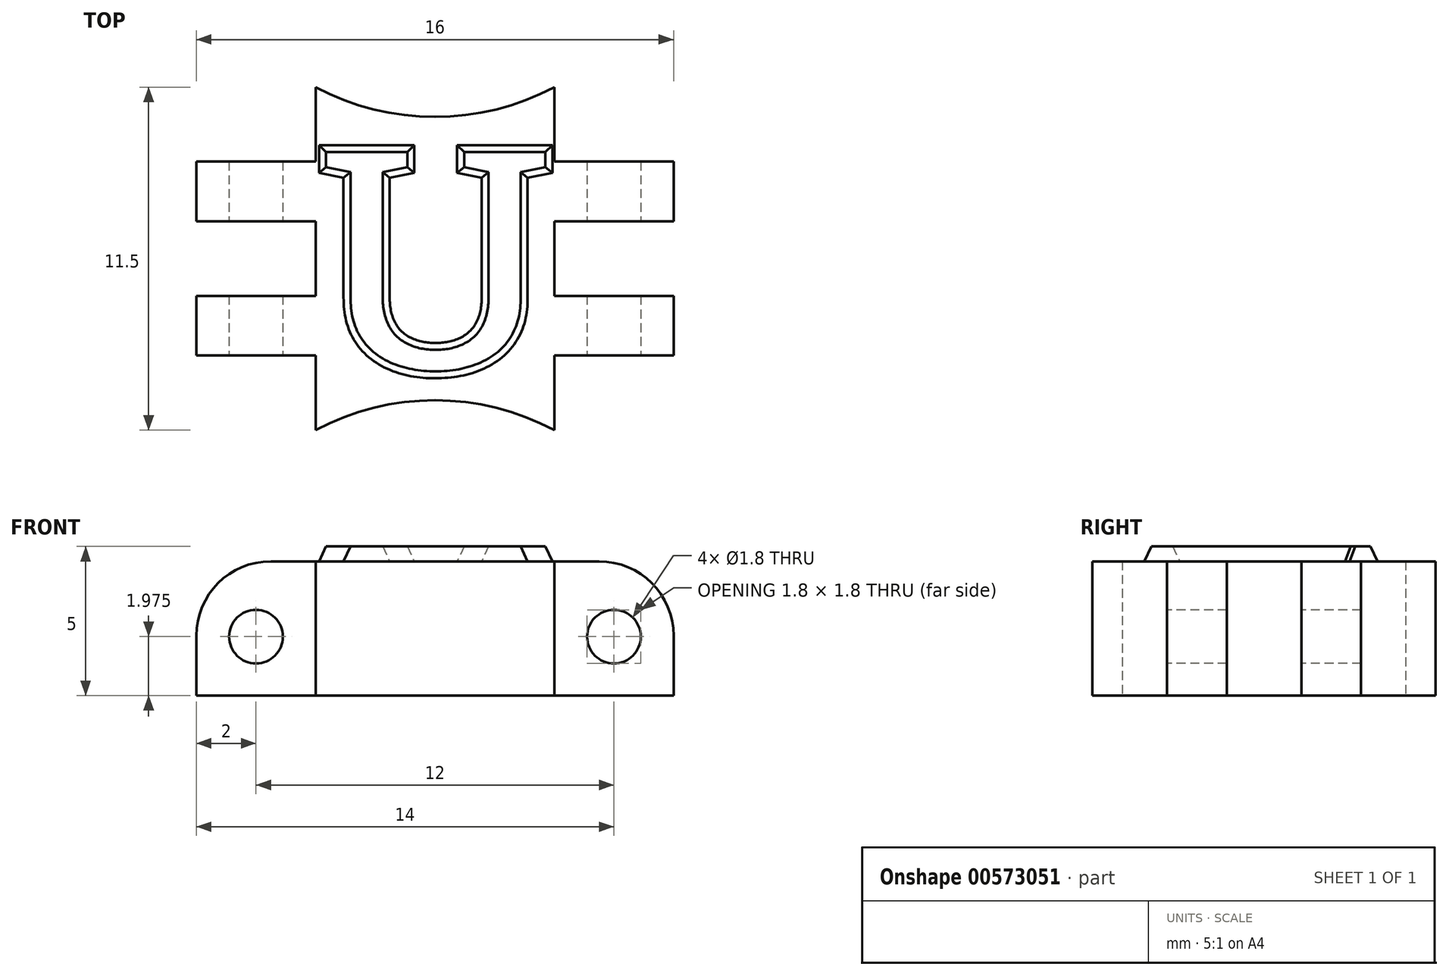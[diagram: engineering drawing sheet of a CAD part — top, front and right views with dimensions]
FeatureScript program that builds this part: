
annotation { "Feature Type Name" : "Feature", "Feature Type Description" : "" }
export const myFeature = defineFeature(function(context is Context, id is Id, definition is map)
    precondition{}
    {
        {
            var Q0;
            Q0=qCreatedBy(makeId("Top.planeOp"),FACE);
            var sketch = newSketch(context, id + "F0", { "sketchPlane" : qUnion([Q0])});
            skLineSegment(sketch, "E0", {"start": v(0, 0) * mm, "end": v(0, 9.5) * mm, "construction": true});
            skLineSegment(sketch, "E1", {"start": v(0, 9.5) * mm, "end": v(5.27, 9.5) * mm, "construction": true});
            skArc(sketch, "E2", {"start": v(0, 9.5) * mm, "mid": v(-2.06, 9.75) * mm, "end": v(-4, 10.5) * mm});
            skLineSegment(sketch, "E3", {"start": v(-4, 10.5) * mm, "end": v(-4, 8) * mm});
            skLineSegment(sketch, "E4", {"start": v(-4, 8) * mm, "end": v(-8, 8) * mm});
            skLineSegment(sketch, "E5", {"start": v(-8, 8) * mm, "end": v(-8, 6) * mm});
            skLineSegment(sketch, "E6", {"start": v(-8, 6) * mm, "end": v(-4, 6) * mm});
            skLineSegment(sketch, "E7", {"start": v(-4, 6) * mm, "end": v(-4, 3.5) * mm});
            skLineSegment(sketch, "E8", {"start": v(-4, 3.5) * mm, "end": v(-8, 3.5) * mm});
            skLineSegment(sketch, "E9", {"start": v(-8, 3.5) * mm, "end": v(-8, 1.5) * mm});
            skLineSegment(sketch, "E10", {"start": v(-8, 1.5) * mm, "end": v(-4, 1.5) * mm});
            skLineSegment(sketch, "E11", {"start": v(-4, 1.5) * mm, "end": v(-4, -1) * mm});
            skLineSegment(sketch, "E12", {"start": v(0, 0) * mm, "end": v(6.13, 0) * mm, "construction": true});
            skArc(sketch, "E13", {"start": v(0, 0) * mm, "mid": v(-2.06, -0.25) * mm, "end": v(-4, -1) * mm});
            skLineSegment(sketch, "E14", {"start": v(0, 4.75) * mm, "end": v(-4, 4.75) * mm, "construction": true});
            skArc(sketch, "E15.MirrorCS", {"start": v(0, 0) * mm, "mid": v(2.06, -0.25) * mm, "end": v(4, -1) * mm});
            skLineSegment(sketch, "E16.MirrorCS", {"start": v(4, 1.5) * mm, "end": v(4, -1) * mm});
            skLineSegment(sketch, "E17.MirrorCS", {"start": v(8, 1.5) * mm, "end": v(4, 1.5) * mm});
            skLineSegment(sketch, "E18.MirrorCS", {"start": v(8, 3.5) * mm, "end": v(8, 1.5) * mm});
            skLineSegment(sketch, "E19.MirrorCS", {"start": v(4, 3.5) * mm, "end": v(8, 3.5) * mm});
            skLineSegment(sketch, "E20.MirrorCS", {"start": v(4, 6) * mm, "end": v(4, 3.5) * mm});
            skLineSegment(sketch, "E21.MirrorCS", {"start": v(8, 6) * mm, "end": v(4, 6) * mm});
            skLineSegment(sketch, "E22.MirrorCS", {"start": v(8, 8) * mm, "end": v(8, 6) * mm});
            skLineSegment(sketch, "E23.MirrorCS", {"start": v(4, 8) * mm, "end": v(8, 8) * mm});
            skLineSegment(sketch, "E24.MirrorCS", {"start": v(4, 10.5) * mm, "end": v(4, 8) * mm});
            skArc(sketch, "E25.MirrorCS", {"start": v(0, 9.5) * mm, "mid": v(2.06, 9.75) * mm, "end": v(4, 10.5) * mm});
            skSolve(sketch);
        }
        {
            var Q0;
            Q0 = qSketchRegion(id + "F0", true);
            extrude(context, id + "F1", {"entities" : qUnion([Q0]), "depth" : 4.5 * mm, "offsetDistance" : 25 * mm});
        }
        {
            var Q0;
            Q0=makeQuery(id+"F1.opExtrude","CAP_EDGE",EDGE,{"disambiguationData":[OSD([sQuery(id+"F0.wireOp",EDGE,"E5")])],"isStart":false});
            var Q1;
            Q1=makeQuery(id+"F1.opExtrude","CAP_EDGE",EDGE,{"disambiguationData":[OSD([sQuery(id+"F0.wireOp",EDGE,"E22.MirrorCS")])],"isStart":false});
            var Q2;
            Q2=makeQuery(id+"F1.opExtrude","CAP_EDGE",EDGE,{"disambiguationData":[OSD([sQuery(id+"F0.wireOp",EDGE,"E9")])],"isStart":false});
            var Q3;
            Q3=makeQuery(id+"F1.opExtrude","CAP_EDGE",EDGE,{"disambiguationData":[OSD([sQuery(id+"F0.wireOp",EDGE,"E18.MirrorCS")])],"isStart":false});
            fillet(context, id + "F2", {"entities" : qUnion([Q0, Q1, Q2, Q3]), "radius" : 2.5 * mm, "tangentPropagation" : true, "allowEdgeOverflow" : false});
        }
        {
            var Q0;
            Q0=makeQuery(id+"F1.opExtrude","CAP_FACE",FACE,{"disambiguationData":[OSD([sQuery(id+"F0.wireOp",EDGE,"E2"),sQuery(id+"F0.wireOp",EDGE,"E3"),sQuery(id+"F0.wireOp",EDGE,"E4"),sQuery(id+"F0.wireOp",EDGE,"E5"),sQuery(id+"F0.wireOp",EDGE,"E6"),sQuery(id+"F0.wireOp",EDGE,"E7"),sQuery(id+"F0.wireOp",EDGE,"E8"),sQuery(id+"F0.wireOp",EDGE,"E9"),sQuery(id+"F0.wireOp",EDGE,"E10"),sQuery(id+"F0.wireOp",EDGE,"E11"),sQuery(id+"F0.wireOp",EDGE,"E13"),sQuery(id+"F0.wireOp",EDGE,"E15.MirrorCS"),sQuery(id+"F0.wireOp",EDGE,"E16.MirrorCS"),sQuery(id+"F0.wireOp",EDGE,"E17.MirrorCS"),sQuery(id+"F0.wireOp",EDGE,"E18.MirrorCS"),sQuery(id+"F0.wireOp",EDGE,"E19.MirrorCS"),sQuery(id+"F0.wireOp",EDGE,"E20.MirrorCS"),sQuery(id+"F0.wireOp",EDGE,"E21.MirrorCS"),sQuery(id+"F0.wireOp",EDGE,"E22.MirrorCS"),sQuery(id+"F0.wireOp",EDGE,"E23.MirrorCS"),sQuery(id+"F0.wireOp",EDGE,"E24.MirrorCS"),sQuery(id+"F0.wireOp",EDGE,"E25.MirrorCS")])],"isStart":false});
            var sketch = newSketch(context, id + "F3", { "sketchPlane" : qUnion([Q0])});
            skText(sketch, "E26", { "text": "U", "fontName": "RobotoSlab-Bold.ttf"});
            skLineSegment(sketch, "E27", {"start": v(0.68, 8.48) * mm, "end": v(-0.68, 8.48) * mm});
            skLineSegment(sketch, "E28", {"start": v(0, 8.48) * mm, "end": v(0, 0) * mm, "construction": true});
            const initialGuessF3  = {"E26": [-0.00409, 0.00085, 1, 0, 0.0078]};
            skSetInitialGuess(sketch, initialGuessF3);
            skSolve(sketch);
        }
        {
            var Q0;
            Q0 = qSketchRegion(id + "F3", true);
            extrude(context, id + "F4", {"entities" : qUnion([Q0]), "operationType" : NewBodyOperationType.ADD, "depth" : 0.5 * mm, "offsetDistance" : 25 * mm, "hasDraft" : true, "draftAngle" : 25 * degree, "draftPullDirection" : true});
        }
        {
            var Q0;
            Q0=makeQuery(id+"F1.opExtrude","SWEPT_FACE",FACE,{"disambiguationData":[OSD([sQuery(id+"F0.wireOp",EDGE,"E10")])]});
            var sketch = newSketch(context, id + "F5", { "sketchPlane" : qUnion([Q0])});
            skLineSegment(sketch, "E29", {"start": v(-6, 0) * mm, "end": v(-6, 1.97) * mm, "construction": true});
            skCircle(sketch, "E30", {"center": v(-6, 1.97) * mm, "radius": 0.9 * mm});
            skLineSegment(sketch, "E31", {"start": v(6, 0) * mm, "end": v(6, 1.97) * mm, "construction": true});
            skCircle(sketch, "E32", {"center": v(6, 1.97) * mm, "radius": 0.9 * mm});
            skSolve(sketch);
        }
        {
            var Q0;
            Q0 = qSketchRegion(id + "F5", true);
            extrude(context, id + "F6", {"entities" : qUnion([Q0]), "operationType" : NewBodyOperationType.REMOVE, "oppositeDirection" : true, "depth" : 25 * mm, "offsetDistance" : 25 * mm});
        }
    });
